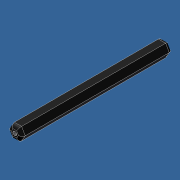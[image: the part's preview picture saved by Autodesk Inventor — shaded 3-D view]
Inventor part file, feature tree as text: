
AUTODESK INVENTOR PART (.ipt)
format: ipt  version: unknown  size: 198,144 bytes
history: native  units: in
note: dims shown in document units (in); Inventor stores cm internally (conversion verified against a paired STEP export)
features: sketch x4, extrude x2, hole x2, fillet x2
ambient origin geometry x8: Origin, YZ Plane, XZ Plane, XY Plane, X Axis, Y Axis, Z Axis, Center Point
bodies: Solid1 (feature_tree)
feature tree (10):
  extrude  "Extrusion1"  Depth=5.975in TaperAngle=0.0deg
  extrude  "Extrusion2"  Depth=0.1in TaperAngle=0.0deg
  hole  "Hole1"  [1 undecoded]
  hole  "Hole2"  [1 undecoded]
  fillet  "Fillet1"  [1 undecoded]
  fillet  "Fillet2"  [1 undecoded]
  sketch  "Sketch1"  dims[d0=0.5in d1=5.975in d2=0.0in]
  sketch  "Sketch2"  dims[d3=0.1in d4=0.1in d5=0.0in]
  sketch  "Sketch3"  dims[d6=0.156in d7=0.75in d8=0.375in d9=0.25in d10=0.5635in d11=1.0in d12=0.8108in]
  sketch  "Sketch4"  dims[d13=0.156in d14=0.75in d15=0.375in d16=0.25in d17=0.5635in d18=1.0in d19=0.8108in d20=0.125in d21=0.125in]
note: 4 required parameter values undecoded (feature->parameter linkage not recoverable at this tier; creation-order binding heuristic only, values carry confidence <= 0.55)
